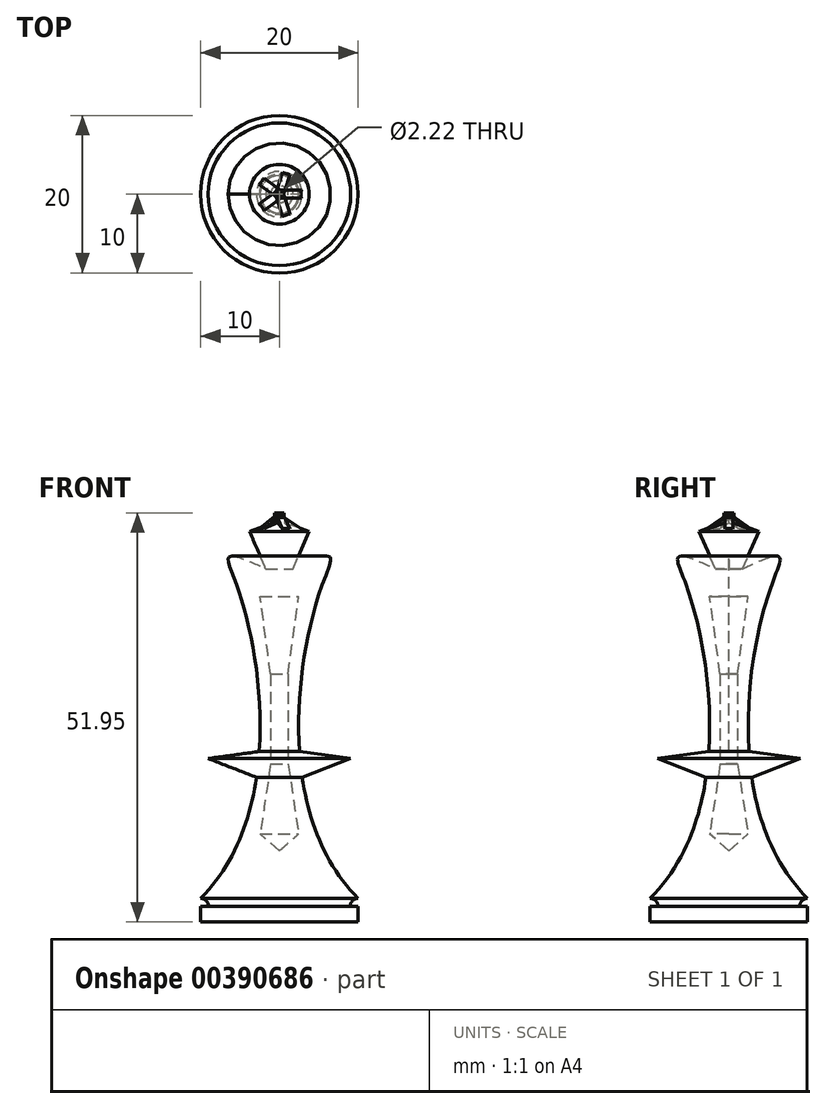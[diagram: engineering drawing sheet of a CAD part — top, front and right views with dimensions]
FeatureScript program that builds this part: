
annotation { "Feature Type Name" : "Feature", "Feature Type Description" : "" }
export const myFeature = defineFeature(function(context is Context, id is Id, definition is map)
    precondition{}
    {
        {
            var Q0;
            Q0=qCreatedBy(makeId("Front.planeOp"),FACE);
            var sketch = newSketch(context, id + "F0", { "sketchPlane" : qUnion([Q0])});
            skLineSegment(sketch, "E0", {"start": v(0, 0) * mm, "end": v(10, 0) * mm});
            skLineSegment(sketch, "E1", {"start": v(10, 0) * mm, "end": v(10, 2) * mm});
            skLineSegment(sketch, "E2", {"start": v(10, 2) * mm, "end": v(9, 2) * mm});
            skPoint(sketch, "E3.endSnap0", {"position": v(10, 1) * mm});
            skArc(sketch, "E4", {"start": v(9, 2) * mm, "mid": v(9.3, 2.7) * mm, "end": v(10, 3) * mm});
            skFitSpline(sketch, "E5", {"points": [v(10, 3) * mm, v(5.64, 43.42) * mm, v(0, 44) * mm], "startDerivative": vector(-45.6, 45.73) * mm, "endDerivative": vector(-88.82, -44.91) * mm});
            skLineSegment(sketch, "E6", {"start": v(0, 0) * mm, "end": v(0, 44) * mm});
            skLineSegment(sketch, "E7", {"start": v(0, 44) * mm, "end": v(0, 51) * mm});
            skPoint(sketch, "E8.endSnap0", {"position": v(0, 22) * mm});
            skLineSegment(sketch, "E9", {"start": v(0, 22) * mm, "end": v(9.06, 20.77) * mm});
            skLineSegment(sketch, "E10", {"start": v(9.06, 20.77) * mm, "end": v(0, 17.25) * mm});
            skLineSegment(sketch, "E11", {"start": v(0, 51) * mm, "end": v(3.79, 49.6) * mm});
            skLineSegment(sketch, "E12", {"start": v(3.79, 49.6) * mm, "end": v(0.8, 42.7) * mm});
            skLineSegment(sketch, "E13", {"start": v(0, 41.33) * mm, "end": v(2.44, 41.33) * mm});
            skLineSegment(sketch, "E14", {"start": v(2.44, 41.33) * mm, "end": v(1.11, 31.5) * mm});
            skLineSegment(sketch, "E15", {"start": v(1.11, 31.5) * mm, "end": v(1.11, 20.07) * mm});
            skLineSegment(sketch, "E16", {"start": v(1.11, 20.07) * mm, "end": v(2.44, 11.16) * mm});
            skLineSegment(sketch, "E17", {"start": v(2.44, 11.16) * mm, "end": v(0, 9.04) * mm});
            skSolve(sketch);
        }
        {
            var Q0;
            {var subQ0=sQuery(id+"F0.wireOp",EDGE,"E0");Q0=makeQuery(id+"F0.imprint","IMPRINT",FACE,{"disambiguationData":[TD([[makeQuery(id+"F0.imprint","IMPRINT",EDGE,{"derivedFrom":subQ0}),1.0]])]});}
            var Q1;
            {var subQ0=sQuery(id+"F0.wireOp",EDGE,"E7");Q1=makeQuery(id+"F0.imprint","IMPRINT",FACE,{"disambiguationData":[TD([[makeQuery(id+"F0.imprint","IMPRINT",EDGE,{"derivedFrom":subQ0}),-1.0]])]});}
            var Q2;
            {var subQ0=sQuery(id+"F0.wireOp",EDGE,"E6");var subQ3=sQuery(id+"F0.wireOp",EDGE,"UrGRKQzg-VSOa-ZteD-O5Gp-x69Zk8rxus1x");var subQ5=makeQuery(id+"F0.imprint","INTERSECT",VERTEX,{"derivedFrom":[subQ0,subQ3]});Q2=makeQuery(id+"F0.imprint","IMPRINT",FACE,{"disambiguationData":[TD([[makeQuery(id+"F0.imprint","IMPRINT",EDGE,{"disambiguationData":[TD([[subQ5,-1.0]])],"derivedFrom":subQ3}),1.0]])]});}
            var Q3;
            {var subQ0=sQuery(id+"F0.wireOp",EDGE,"E10");var subQ1=sQuery(id+"F0.wireOp",EDGE,"E5");var subQ2=makeQuery(id+"F0.imprint","INTERSECT",VERTEX,{"derivedFrom":[subQ1,subQ0]});Q3=makeQuery(id+"F0.imprint","IMPRINT",FACE,{"disambiguationData":[TD([[makeQuery(id+"F0.imprint","IMPRINT",EDGE,{"disambiguationData":[TD([[subQ2,-1.0]])],"derivedFrom":subQ1}),1.0]])]});}
            var Q4;
            {var subQ0=sQuery(id+"F0.wireOp",EDGE,"E10");var subQ1=sQuery(id+"F0.wireOp",EDGE,"E5");var subQ2=makeQuery(id+"F0.imprint","INTERSECT",VERTEX,{"derivedFrom":[subQ1,subQ0]});Q4=makeQuery(id+"F0.imprint","IMPRINT",FACE,{"disambiguationData":[TD([[makeQuery(id+"F0.imprint","IMPRINT",EDGE,{"disambiguationData":[TD([[subQ2,-1.0]])],"derivedFrom":subQ1}),-1.0]])]});}
            var Q5;
            {var subQ0=sQuery(id+"F0.wireOp",EDGE,"E9");var subQ1=sQuery(id+"F0.wireOp",EDGE,"E5");var subQ2=makeQuery(id+"F0.imprint","INTERSECT",VERTEX,{"derivedFrom":[subQ1,subQ0]});Q5=makeQuery(id+"F0.imprint","IMPRINT",FACE,{"disambiguationData":[TD([[makeQuery(id+"F0.imprint","IMPRINT",EDGE,{"disambiguationData":[TD([[subQ2,-1.0]])],"derivedFrom":subQ1}),1.0]])]});}
            var Q6;
            Q6=sQuery(id+"F0.wireOp",EDGE,"E6");
            revolve(context, id + "F1", {"entities" : qUnion([Q0, Q1, Q2, Q3, Q4, Q5]), "axis" : qUnion([Q6]), "revolveType" : RevolveType.FULL});
        }
        {
            var Q0;
            Q0=qCreatedBy(makeId("Front.planeOp"),FACE);
            var sketch = newSketch(context, id + "F2", { "sketchPlane" : qUnion([Q0])});
            skLineSegment(sketch, "E18", {"start": v(-0.36, 50.84) * mm, "end": v(-0.36, 51.95) * mm});
            skLineSegment(sketch, "E19", {"start": v(-0.36, 51.95) * mm, "end": v(3.47, 49.53) * mm});
            skLineSegment(sketch, "E20", {"start": v(3.47, 49.53) * mm, "end": v(-0.36, 50.84) * mm});
            skSolve(sketch);
        }
        {
            var Q0;
            Q0=makeQuery(id+"F2.imprint","IMPRINT",FACE,{"disambiguationData":[TD([[makeQuery(id+"F2.imprint","IMPRINT",EDGE,{"derivedFrom":sQuery(id+"F2.wireOp",EDGE,"E18")}),-1.0]])]});
            extrude(context, id + "F3", {"entities" : qUnion([Q0]), "endBound" : BoundingType.SYMMETRIC, "depth" : 1 * mm});
        }
        {
            var Q0;
            Q0=makeQuery(id+"F3.opExtrude","SWEPT_BODY",BODY,{"disambiguationData":[OSD([sQuery(id+"F2.wireOp",EDGE,"E18"),sQuery(id+"F2.wireOp",EDGE,"E19"),sQuery(id+"F2.wireOp",EDGE,"E20")])]});
            var Q1;
            Q1=sQuery(id+"F0.wireOp",EDGE,"E7");
            circularPattern(context, id + "F4", {"operationType" : NewBodyOperationType.ADD, "entities" : qUnion([Q0]), "axis" : qUnion([Q1]), "angle" : 360 * degree, "instanceCount" : 5, "equalSpace" : true});
        }
    });
